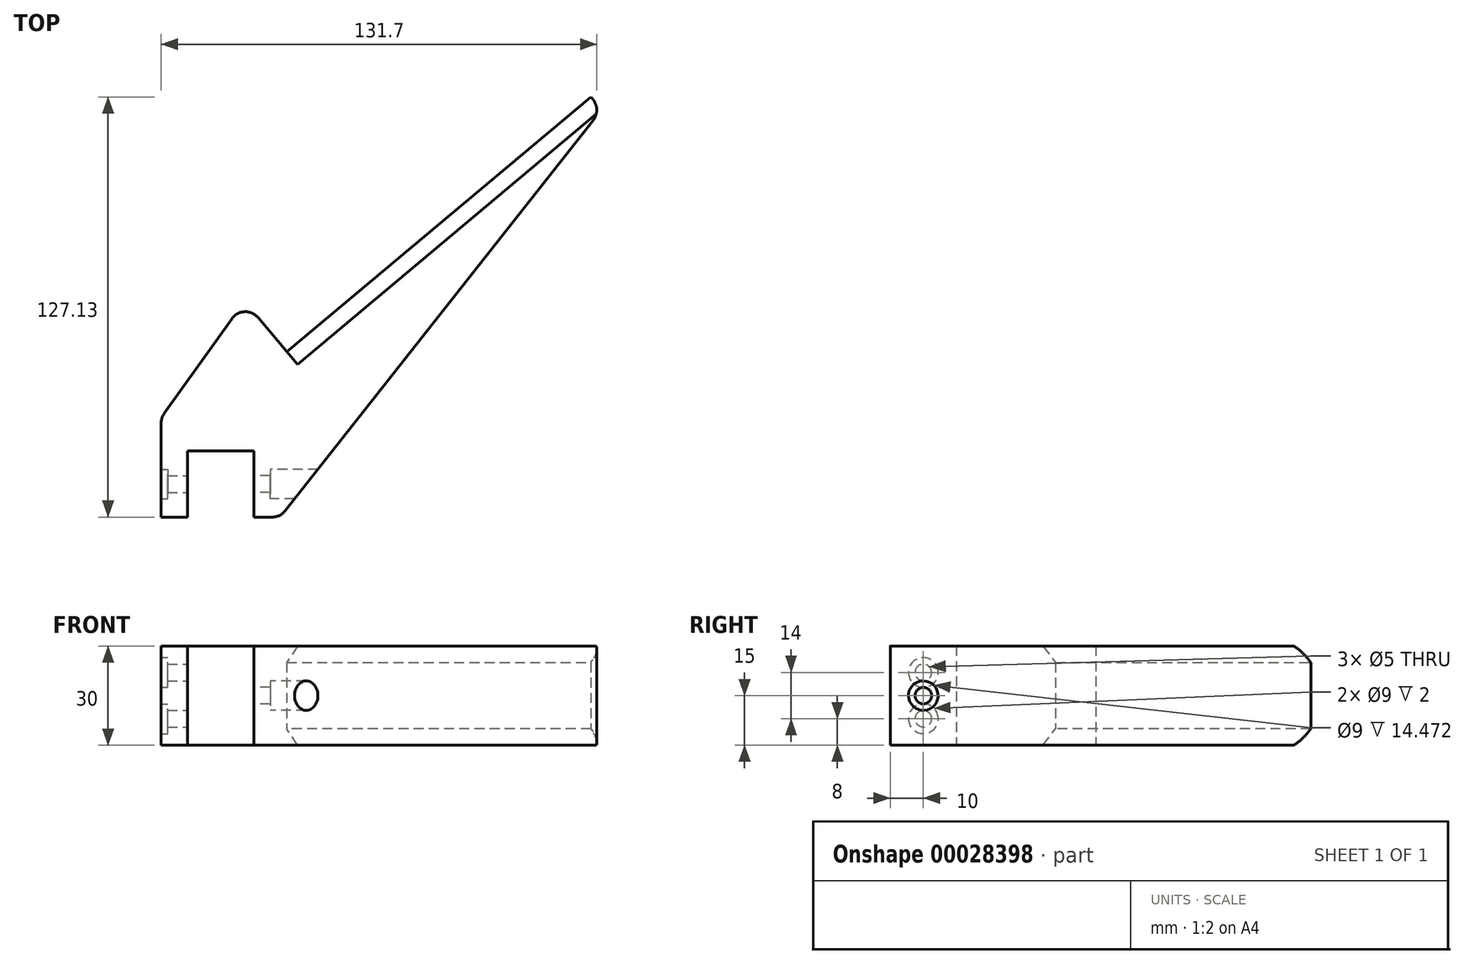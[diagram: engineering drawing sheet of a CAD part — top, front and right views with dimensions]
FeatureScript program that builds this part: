
annotation { "Feature Type Name" : "Feature", "Feature Type Description" : "" }
export const myFeature = defineFeature(function(context is Context, id is Id, definition is map)
    precondition{}
    {
        {
            var Q0;
            Q0=qCreatedBy(makeId("Top.planeOp"),FACE);
            var sketch = newSketch(context, id + "F0", { "sketchPlane" : qUnion([Q0])});
            skLineSegment(sketch, "E0", {"start": v(0, 0) * mm, "end": v(0, -20) * mm});
            skLineSegment(sketch, "E1", {"start": v(0, -20) * mm, "end": v(-8, -20) * mm});
            skLineSegment(sketch, "E2", {"start": v(0, 0) * mm, "end": v(20, 0) * mm});
            skLineSegment(sketch, "E3", {"start": v(20, 0) * mm, "end": v(20, -20) * mm});
            skLineSegment(sketch, "E4", {"start": v(20, -20) * mm, "end": v(28, -20) * mm});
            skLineSegment(sketch, "E5", {"start": v(28, -20) * mm, "end": v(125.14, 103.3) * mm});
            skLineSegment(sketch, "E6", {"start": v(125.14, 103.3) * mm, "end": v(121.93, 107.13) * mm});
            skLineSegment(sketch, "E7", {"start": v(121.93, 107.13) * mm, "end": v(30, 30) * mm});
            skLineSegment(sketch, "E8", {"start": v(30, 30) * mm, "end": v(17.14, 45.32) * mm});
            skLineSegment(sketch, "E9", {"start": v(17.14, 45.32) * mm, "end": v(-8, 10) * mm});
            skLineSegment(sketch, "E10", {"start": v(-8, 10) * mm, "end": v(-8, -20) * mm});
            skLineSegment(sketch, "E11", {"start": v(30, 72.38) * mm, "end": v(30, 30) * mm, "construction": true});
            skLineSegment(sketch, "E12", {"start": v(-50.35, 125.76) * mm, "end": v(142.49, -104.06) * mm, "construction": true});
            skLineSegment(sketch, "E13", {"start": v(30, 30) * mm, "end": v(46.07, 10.85) * mm, "construction": true});
            skLineSegment(sketch, "E14", {"start": v(-50.35, 125.76) * mm, "end": v(33.92, 196.46) * mm, "construction": true});
            skLineSegment(sketch, "E15", {"start": v(33.92, 196.46) * mm, "end": v(226.75, -33.35) * mm, "construction": true});
            skLineSegment(sketch, "E16", {"start": v(226.75, -33.35) * mm, "end": v(142.49, -104.06) * mm, "construction": true});
            skSolve(sketch);
        }
        {
            var Q0;
            Q0 = qSketchRegion(id + "F0", true);
            extrude(context, id + "F1", {"entities" : qUnion([Q0]), "depth" : 30 * mm});
        }
        {
            var Q0;
            Q0=makeQuery(id+"F1.opExtrude","SWEPT_FACE",FACE,{"disambiguationData":[OSD([sQuery(id+"F0.wireOp",EDGE,"E3")])]});
            var sketch = newSketch(context, id + "F2", { "sketchPlane" : qUnion([Q0])});
            skLineSegment(sketch, "E17.0.0", {"start": v(0, 0) * mm, "end": v(20, 0) * mm});
            skLineSegment(sketch, "E17.0.1", {"start": v(20, 0) * mm, "end": v(20, 30) * mm});
            skLineSegment(sketch, "E17.0.2", {"start": v(20, 30) * mm, "end": v(0, 30) * mm});
            skLineSegment(sketch, "E17.0.3", {"start": v(0, 30) * mm, "end": v(0, 0) * mm});
            skLineSegment(sketch, "E18", {"start": v(0, 30) * mm, "end": v(20, 0) * mm, "construction": true});
            skPoint(sketch, "E19", {"position": v(10, 15) * mm});
            skCircle(sketch, "E20", {"center": v(10, 15) * mm, "radius": 4.5 * mm});
            skCircle(sketch, "E21", {"center": v(10, 15) * mm, "radius": 2.5 * mm});
            skSolve(sketch);
        }
        {
            var Q0;
            Q0=makeQuery(id+"F2.imprint","IMPRINT",FACE,{"disambiguationData":[TD([[makeQuery(id+"F2.imprint","IMPRINT",EDGE,{"derivedFrom":sQuery(id+"F2.wireOp",EDGE,"E20")}),1.0]])]});
            var Q1;
            Q1=makeQuery(id+"F2.imprint","IMPRINT",FACE,{"disambiguationData":[TD([[makeQuery(id+"F2.imprint","IMPRINT",EDGE,{"derivedFrom":sQuery(id+"F2.wireOp",EDGE,"E21")}),1.0]])]});
            extrude(context, id + "F3", {"entities" : qUnion([Q0, Q1]), "operationType" : NewBodyOperationType.REMOVE, "oppositeDirection" : true, "depth" : 25 * mm});
        }
        {
            var Q0;
            Q0=makeQuery(id+"F2.imprint","IMPRINT",FACE,{"disambiguationData":[TD([[makeQuery(id+"F2.imprint","IMPRINT",EDGE,{"derivedFrom":sQuery(id+"F2.wireOp",EDGE,"E20")}),1.0]])]});
            extrude(context, id + "F4", {"entities" : qUnion([Q0]), "operationType" : NewBodyOperationType.ADD, "oppositeDirection" : true, "depth" : 5 * mm});
        }
        {
            var Q0;
            Q0=makeQuery(id+"F1.opExtrude","SWEPT_FACE",FACE,{"disambiguationData":[OSD([sQuery(id+"F0.wireOp",EDGE,"E0")])]});
            var sketch = newSketch(context, id + "F5", { "sketchPlane" : qUnion([Q0])});
            skLineSegment(sketch, "E22.0.0", {"start": v(-20, 0) * mm, "end": v(0, 0) * mm});
            skLineSegment(sketch, "E22.0.1", {"start": v(0, 0) * mm, "end": v(0, 30) * mm});
            skLineSegment(sketch, "E22.0.2", {"start": v(0, 30) * mm, "end": v(-20, 30) * mm});
            skLineSegment(sketch, "E22.0.3", {"start": v(-20, 30) * mm, "end": v(-20, 0) * mm});
            skLineSegment(sketch, "E23", {"start": v(0, 30) * mm, "end": v(-20, 0) * mm, "construction": true});
            skPoint(sketch, "E24", {"position": v(-10, 15) * mm});
            skLineSegment(sketch, "E25", {"start": v(-10, 15) * mm, "end": v(-10, 22) * mm, "construction": true});
            skLineSegment(sketch, "E26", {"start": v(-10, 15) * mm, "end": v(-10, 8) * mm, "construction": true});
            skCircle(sketch, "E27", {"center": v(-10, 22) * mm, "radius": 2.5 * mm});
            skCircle(sketch, "E28", {"center": v(-10, 22) * mm, "radius": 4.5 * mm});
            skCircle(sketch, "E29", {"center": v(-10, 8) * mm, "radius": 2.5 * mm});
            skCircle(sketch, "E30", {"center": v(-10, 8) * mm, "radius": 4.5 * mm});
            skSolve(sketch);
        }
        {
            var Q0;
            Q0=makeQuery(id+"F5.imprint","IMPRINT",FACE,{"disambiguationData":[TD([[makeQuery(id+"F5.imprint","IMPRINT",EDGE,{"derivedFrom":sQuery(id+"F5.wireOp",EDGE,"E27")}),-1.0]])]});
            var Q1;
            Q1=makeQuery(id+"F5.imprint","IMPRINT",FACE,{"disambiguationData":[TD([[makeQuery(id+"F5.imprint","IMPRINT",EDGE,{"derivedFrom":sQuery(id+"F5.wireOp",EDGE,"E27")}),1.0]])]});
            var Q2;
            Q2=makeQuery(id+"F5.imprint","IMPRINT",FACE,{"disambiguationData":[TD([[makeQuery(id+"F5.imprint","IMPRINT",EDGE,{"derivedFrom":sQuery(id+"F5.wireOp",EDGE,"E29")}),-1.0]])]});
            var Q3;
            Q3=makeQuery(id+"F5.imprint","IMPRINT",FACE,{"disambiguationData":[TD([[makeQuery(id+"F5.imprint","IMPRINT",EDGE,{"derivedFrom":sQuery(id+"F5.wireOp",EDGE,"E29")}),1.0]])]});
            extrude(context, id + "F6", {"entities" : qUnion([Q0, Q1, Q2, Q3]), "operationType" : NewBodyOperationType.REMOVE, "oppositeDirection" : true, "depth" : 25 * mm});
        }
        {
            var Q0;
            Q0=makeQuery(id+"F5.imprint","IMPRINT",FACE,{"disambiguationData":[TD([[makeQuery(id+"F5.imprint","IMPRINT",EDGE,{"derivedFrom":sQuery(id+"F5.wireOp",EDGE,"E27")}),-1.0]])]});
            var Q1;
            Q1=makeQuery(id+"F5.imprint","IMPRINT",FACE,{"disambiguationData":[TD([[makeQuery(id+"F5.imprint","IMPRINT",EDGE,{"derivedFrom":sQuery(id+"F5.wireOp",EDGE,"E29")}),-1.0]])]});
            extrude(context, id + "F7", {"entities" : qUnion([Q0, Q1]), "operationType" : NewBodyOperationType.ADD, "oppositeDirection" : true, "depth" : 6 * mm});
        }
        {
            var Q0;
            Q0=makeQuery(id+"F1.opExtrude","SWEPT_EDGE",EDGE,{"disambiguationData":[OSD([sQuery(id+"F0.wireOp",EDGE,"E8"),sQuery(id+"F0.wireOp",EDGE,"E9")])]});
            var Q1;
            Q1=makeQuery(id+"F1.opExtrude","SWEPT_EDGE",EDGE,{"disambiguationData":[OSD([sQuery(id+"F0.wireOp",EDGE,"E9"),sQuery(id+"F0.wireOp",EDGE,"E10")])]});
            var Q2;
            Q2=makeQuery(id+"F1.opExtrude","SWEPT_EDGE",EDGE,{"disambiguationData":[OSD([sQuery(id+"F0.wireOp",EDGE,"E4"),sQuery(id+"F0.wireOp",EDGE,"E5")])]});
            var Q3;
            Q3=makeQuery(id+"F1.opExtrude","SWEPT_EDGE",EDGE,{"disambiguationData":[OSD([sQuery(id+"F0.wireOp",EDGE,"E5"),sQuery(id+"F0.wireOp",EDGE,"E6")])]});
            fillet(context, id + "F8", {"entities" : qUnion([Q0, Q1, Q2, Q3]), "radius" : 5 * mm, "tangentPropagation" : true, "allowEdgeOverflow" : false});
        }
        {
            var Q0;
            Q0=makeQuery(id+"F1.opExtrude","CAP_EDGE",EDGE,{"disambiguationData":[OSD([sQuery(id+"F0.wireOp",EDGE,"E7")])],"isStart":false});
            var Q1;
            Q1=makeQuery(id+"F1.opExtrude","CAP_EDGE",EDGE,{"disambiguationData":[OSD([sQuery(id+"F0.wireOp",EDGE,"E7")])],"isStart":true});
            chamfer(context, id + "F9", {"entities" : qUnion([Q0, Q1]), "width" : 5 * mm, "tangentPropagation" : true});
        }
    });
